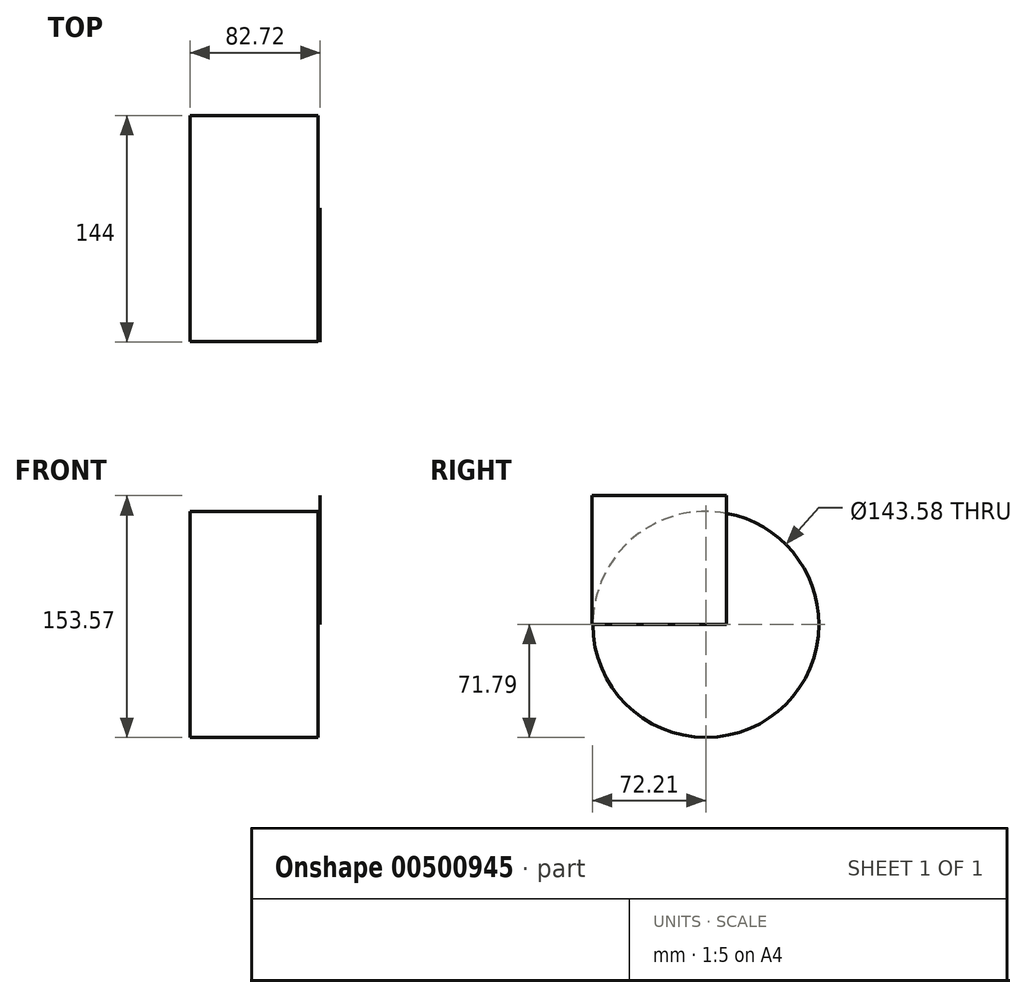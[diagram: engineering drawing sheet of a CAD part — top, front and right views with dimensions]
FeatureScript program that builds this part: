
annotation { "Feature Type Name" : "Feature", "Feature Type Description" : "" }
export const myFeature = defineFeature(function(context is Context, id is Id, definition is map)
    precondition{}
    {
        {
            var Q0;
            Q0=qCreatedBy(makeId("Right.planeOp"),FACE);
            var sketch = newSketch(context, id + "F0", { "sketchPlane" : qUnion([Q0])});
            skCircle(sketch, "E0", {"center": v(0, 0) * mm, "radius": 71.8 * mm});
            skSolve(sketch);
        }
        {
            var Q0;
            Q0=sQuery(id+"F0.wireOp",EDGE,"E0");
            extrude(context, id + "F1", {"bodyType" : ToolBodyType.SURFACE, "surfaceEntities" : qUnion([Q0]), "endBound" : BoundingType.SYMMETRIC, "oppositeDirection" : true, "depth" : 81.45 * mm});
        }
        {
            var Q0;
            Q0=qCreatedBy(makeId("Top.planeOp"),FACE);
            var sketch = newSketch(context, id + "F2", { "sketchPlane" : qUnion([Q0])});
            skLineSegment(sketch, "E1", {"start": v(42, 13.04) * mm, "end": v(42, -72.21) * mm});
            skLineSegment(sketch, "E2", {"start": v(42, -72.21) * mm, "end": v(59.42, -103.99) * mm});
            skLineSegment(sketch, "E3", {"start": v(59.42, -103.99) * mm, "end": v(42, -72.21) * mm});
            skSolve(sketch);
        }
        {
            var Q0;
            Q0=sQuery(id+"F2.wireOp",EDGE,"E1");
            extrude(context, id + "F3", {"bodyType" : ToolBodyType.SURFACE, "surfaceEntities" : qUnion([Q0]), "depth" : 81.78 * mm});
        }
    });
